# Revit family: LAMP_OCULT SYSTEM DOWNLIGHT (DALI)
name_source: partatom
category: Luminarias
revit_build: Autodesk Revit 2015 (Build: 20140606_1530(x64)
units: mm (PartAtom-declared; Revit-internal decimal feet)

## types (16) — shared parameters
CRI = 80
Comentarios de tipo = Availability of changing profile version and height when placed in project.
Elevación por defecto = 1219 mm
Fabricante = LAMP
Finish = Matte black RAL 9011
Height = 400 mm  [stored 1.31234 ft]
IEE = A+
Installation instructions = https://www.lamp.es
Insulation class = I
LED Lifetime = 50.000 L80 B10
Lamp = HIGH POWER LED
Luminaire type = Downlight
MacAdam = 3
Manufacturer URL = http://www.lamp.es
Manufacturer country = Spain
Manufacturer name = LAMP
Material perfil = LAMP_Aluminio Ocult Pendular NG
Material suspension = Panel de metal
Model explanation = Availability of changing profile version and height when placed in project.
Product URL = https://www.lamp.es
Product datasheet = http://www.lamp.es
Protection rating = IP20
Type = HIGH POWER NICHIA

## per-type parameters (varying)
| type | Descripción | Dimensions | Efficacy | Gear | Initial color | Initial intensity | Last update | Length | Modelo | Number of reflectors | Photometric web file | Plum | Power | Power Supply | Product code | UGR | Weight |
| 3 540LM 3000 MEDIUM FLOOD | OCULT SYS. DOWN. 3 600 WW MFL DALI BK. | 400 | 73 lm/W | Adjustable DALI | 3000 K | 540 lm | 31/07/2019 | 400 mm  [stored 1.31234 ft] | OS1DO306MF830DB | 3 | Modulo downlight : 3 540LM 3000 MEDIUM FLOOD | 7 W | 6 W | 100-240V 50/60Hz | OS1DO306MF830DB | 3 | 0.57 kg |
| 3 540LM 4000 MEDIUM FLOOD | OCULT SYS. DOWN. 3 600 NW MFL DALI BK. | 400 | 73 lm/W | Adjustable DALI | 4000 K | 540 lm | 31/07/2019 | 400 mm  [stored 1.31234 ft] | OS1DO306MF840DB | 3 | Modulo downlight : 3 540LM 4000 MEDIUM FLOOD | 7 W | 6 W | 100-277V 50/60Hz | OS1DO306MF840DB | 3 | 0.57 kg |
| 3 549LM 3000 WIDE FLOOD | OCULT SYS. DOWN. 3 600 WW WFL DALI BK. | 400 | 74 lm/W | Adjustable DALI | 3000 K | 549 lm | 31/07/2019 | 400 mm  [stored 1.31234 ft] | OS1DO306WF830DB | 3 | Modulo downlight : 3 549LM 3000 WIDE FLOOD | 7 W | 6 W | 100-277V 50/60Hz | OS1DO306WF830DB | 16 | 0.57 kg |
| 3 549LM 4000 WIDE FLOOD | OCULT SYS. DOWN. 3 600 NW WFL DALI BK.
OCULT SYS. DOWN. 3 600 NW WFL DALI BK.
OCULT SYS. DOWN. 3 600 NW WFL DALI BK. | 400 | 74 lm/W | Adjustable DALI | 4000 K | 549 lm | 31/07/2019 | 400 mm  [stored 1.31234 ft] | OS1DO306WF840DB | 3 | Modulo downlight : 3 549LM 4000 WIDE FLOOD | 7 W | 6 W | 100-277V 50/60Hz | OS1DO306WF840DB | 16 | 0.57 kg |
| 6 1080LM 3000 MEDIUM FLOOD | OCULT SYS. DOWN. 6 1200 WW MFL DALI BK. | 500 | 82 lm/W | Adjutable DALI | 3000 K | 1080 lm | 31/07/2019 | 498 mm  [stored 1.63386 ft] | OS1DO612MF830DB | 6 | Modulo downlight : 6 1080LM 3000 MEDIUM FLOOD | 13 W | 12 W | 100-277V 50/60Hz | OS1DO612MF830DB | 3 | 0.72 kg |
| 6 1080LM 4000 MEDIUM FLOOD | OCULT SYS. DOWN. 6 1200 NW MFL DALI BK. | 500 | 82 lm/W | Adjustable DALI | 4000 K | 1080 lm | 31/07/2019 | 498 mm  [stored 1.63386 ft] | OS1DO612MF840DB
OS1DO612MF840DB | 6 | Modulo downlight : 6 1080LM 4000 MEDIUM FLOOD | 13 W | 12 W | 100-277V 50/60Hz | OS1DO612MF840DB
OS1DO612MF840DB | 3 | 0.72 kg |
| 6 1098LM 3000 WIDE FLOOD | OCULT SYS. DOWN. 6 1200 WW WFL DALI BK. | 500 | 84 lm/W | Adjustable DALI | 3000 K | 1098 lm | 05/07/2019 | 498 mm  [stored 1.63386 ft] | OS1DO612WF830DB | 6 | Modulo downlight : 6 1098LM 3000 WIDE FLOOD | 13 W | 12 W | 100-277V 50/60Hz | OS1DO612WF830DB | 16 | 0.72 kg |
| 6 1098LM 4000 WIDE FLOOD | OCULT SYS. DOWN. 6 1200 NW WFL DALI BK. | 500 | 84 lm/W | Adjustable DALI | 4000 K | 1098 lm | 31/07/2019 | 498 mm  [stored 1.63386 ft] | OS1DO612WF840DB
OS1DO612WF840DB | 6 | Modulo downlight : 6 1098LM 4000 WIDE FLOOD | 13 W | 12 W | 100-277V 50/60Hz | OS1DO612WF840DB
OS1DO612WF840DB | 16 | 0.72 kg |
| 9 1620LM 3000 MEDIUM FLOOD | OCULT SYS. DOWN. 9 1800 WW MFL DALI BK. | 600 | 78 lm/W | Adjustable DALI | 3000 K | 1620 lm | 31/07/2019 | 597 mm | OS1DO918MF830DB | 9 | Modulo downlight : 9 1620LM 3000 MEDIUM FLOOD | 21 W | 18 W | 100-277V 50/60Hz | OS1DO918MF830DB | 3 | 1.01 kg |
| 9 1620LM 4000 MEDIUM FLOOD | OCULT SYS. DOWN. 9 1800 NW MFL DALI BK. | 600 | 78 lm/W | Adjustable DALI | 4000 K | 1620 lm | 31/07/2019 | 597 mm | OS1DO918MF840DB | 9 | Modulo downlight : 9 1620LM 4000 MEDIUM FLOOD | 21 W | 18 W | 100-277V 50/60Hz | OS1DO918MF840DB | 3 | 1.01 kg |
| 9 1647LM 3000 WIDE FLOOD | OCULT SYS. DOWN. 9 1800 WW WFL DALI BK. | 600 | 79 lm/W | Adjustable DALI | 3000 K | 1647 lm | 31/07/2019 | 597 mm | OS1DO918WF830DB | 9 | Modulo downlight : 9 1647LM 3000 WIDE FLOOD | 21 W | 18 W | 100-277V 50/60Hz | OS1DO918WF830DB | 16 | 1.01 kg |
| 9 1647LM 4000 WIDE FLOOD | OCULT SYS. DOWN. 9 1800 NW WFL DALI BK. | 600 | 79 lm/W | Adjustable DALI | 4000 K | 1647 lm | 31/07/2019 | 597 mm | OS1DO918WF840DB | 9 | Modulo downlight : 9 1647LM 4000 WIDE FLOOD | 21 W | 18 W | 100-277V 50/60Hz | OS1DO918WF840DB | 16 | 1.01 kg |
| 12 2160LM 3000 MEDIUM FLOOD | OCULT SYS. DOWN. 12 2400 WW MFL DALI BK | 700 | 80 lm/W | Adjustable DALI | 3000 K | 2160 lm | 31/07/2019 | 696 mm  [stored 2.28346 ft] | OS1DO1222MF830DB | 12 | Modulo downlight : 12 2160LM 3000 MEDIUM FLOOD | 27 W | 24 W | 220-240V 50/60Hz | OS1DO1222MF830DB | 3 | 1.26 kg |
| 12 2160LM 4000 MEDIUM FLOOD | OCULT SYS. DOWN. 12 2400 NW MFL DALI BK | 700 | 80 lm/W | Adjustable DALI | 4000 K | 2160 lm | 31/07/2019 | 696 mm  [stored 2.28346 ft] | OS1DO1222MF840DB | 12 | Modulo downlight : 12 2160LM 4000 MEDIUM FLOOD | 27 W | 24 W | 220-240V 50/60Hz | OS1DO1222MF840DB | 3 | 1.26 kg |
| 12 2196LM 3000 WIDE FLOOD | OCULT SYS. DOWN. 12 2400 WW WFL DALI BK | 700 | 82 lm/W | Adjustable DALI | 3000 K | 2196 lm | 31/07/2019 | 696 mm  [stored 2.28346 ft] | OS1DO1222WF830DB | 12 | Modulo downlight : 12 2196LM 3000 WIDE FLOOD | 27 W | 24 W | 220-240V 50/60Hz | OS1DO1222WF830DB | 16 | 1.26 kg |
| 12 2196LM 4000 WIDE FLOOD | OCULT SYS. DOWN. 12 2400 NW WFL DALI BK | 700 | 82 lm/W | Adjustable DALI | 4000 K | 2196 lm | 31/07/2019 | 696 mm  [stored 2.28346 ft] | OS1DO1222WF840DB | 12 | Modulo downlight : 12 2196LM 4000 WIDE FLOOD | 27 W | 24 W | 220-240V 50/60Hz | OS1DO1222WF840DB | 16 | 1.26 kg |

note: [stored X ft] marks values corroborated as IEEE doubles in the binary element streams (Revit-internal decimal feet)
